# Revit family: BLE-S-WHS-LED
name_source: partatom
category: Lighting Fixtures
units: mm (PartAtom-declared; Revit-internal decimal feet)

## family parameters
Cut with Voids When Loaded = No
Host = Face
Light Source = Yes
Maintain Annotation Orientation = No
Part Type = Normal
Room Calculation Point = No
Round Connector Dimension = Use Diameter
Shared = No

## types (60) — shared parameters
Actual Stem Length = 1' - 0"
Base Material = 100 - Black
Color Filter = 16777215
Default Elevation = 4' - 0"
Dimming Lamp Color Temperature Shift = <None>
Emit from Line Length = 2' - 0"
Length Calc = 1' - 0"
Max Length = 4' - 0"
Min Length = 0' - 6"
Photometric Web File = generic
Shade Material = 100 - Black
Stem Length Multiplier = 2
Stem Material = 100 - Black
Tilt Angle = 0.00°

## per-type parameters (varying)
| type | 12" | 14" | 16" | 18" | 20" | Base Height | CAN-5001 | Dome | Flat | Heat Sink | Light Source Distance | SHD-0189 | STM-50XX | STM-75XX | SUB-0062 |
| 12" Dome 1/2" Stem Swivel Base | Yes | No | No | No | No | 0' - 5 5/32" | No | Yes | No | 0' - 4 5/8" | 0' - 5 5/8" | No | Yes | No | Yes |
| 14" Dome 1/2" Stem Large Base | No | Yes | No | No | No | 0' - 3 11/32" | No | Yes | No | 0' - 4 7/16" | 0' - 5 5/8" | Yes | Yes | No | No |
| 16" Dome 1/2" Stem Large Base | No | No | Yes | No | No | 0' - 3 11/32" | No | Yes | No | 0' - 4 7/16" | 0' - 5 5/8" | Yes | Yes | No | No |
| 18" Dome 1/2" Stem Large Base | No | No | No | Yes | No | 0' - 3 11/32" | No | Yes | No | 0' - 4 13/32" | 0' - 5 5/8" | Yes | Yes | No | No |
| 20" Dome 1/2" Stem Large Base | No | No | No | No | Yes | 0' - 3 11/32" | No | Yes | No | 0' - 4 13/32" | 0' - 5 5/8" | Yes | Yes | No | No |
| 12" Flat 1/2" Stem Large Base | Yes | No | No | No | No | 0' - 3 11/32" | No | No | Yes | 0' - 4 5/8" | 0' - 5 5/8" | Yes | Yes | No | No |
| 14" Flat 1/2" Stem Large Base | No | Yes | No | No | No | 0' - 3 11/32" | No | No | Yes | 0' - 4 7/16" | 0' - 5 5/8" | Yes | Yes | No | No |
| 16" Flat 1/2" Stem Large Base | No | No | Yes | No | No | 0' - 3 11/32" | No | No | Yes | 0' - 4 7/16" | 0' - 5 5/8" | Yes | Yes | No | No |
| 18" Flat 1/2" Stem Large Base | No | No | No | Yes | No | 0' - 3 11/32" | No | No | Yes | 0' - 4 13/32" | 0' - 5 5/8" | Yes | Yes | No | No |
| 20" Flat 1/2" Stem Large Base | No | No | No | No | Yes | 0' - 3 11/32" | No | No | Yes | 0' - 4 13/32" | 0' - 5 5/8" | Yes | Yes | No | No |
| 12" Dome 1/2" Stem Large Base | Yes | No | No | No | No | 0' - 3 11/32" | No | Yes | No | 0' - 4 5/8" | 1' - 10 5/32" | Yes | Yes | No | No |
| 12" Dome 1/2" Stem Small Base | Yes | No | No | No | No | 0' - 0 27/32" | Yes | Yes | No | 0' - 4 5/8" | 1' - 7 3/32" | No | Yes | No | No |
| 12" Flat 1/2" Stem Small Base | Yes | No | No | No | No | 0' - 0 27/32" | Yes | No | Yes | 0' - 4 5/8" | 0' - 5 5/8" | No | Yes | No | No |
| 12" Flat 1/2" Stem Swivel Base | Yes | No | No | No | No | 0' - 5 5/32" | No | No | Yes | 0' - 4 5/8" | 0' - 5 5/8" | No | Yes | No | Yes |
| 14" Dome 1/2" Stem Small Base | No | Yes | No | No | No | 0' - 0 27/32" | Yes | Yes | No | 0' - 4 7/16" | 0' - 5 5/8" | No | Yes | No | No |
| 14" Dome 1/2" Stem Swivel Base | No | Yes | No | No | No | 0' - 5 5/32" | No | Yes | No | 0' - 4 7/16" | 0' - 5 5/8" | No | Yes | No | Yes |
| 14" Flat 1/2" Stem Small Base | No | Yes | No | No | No | 0' - 0 27/32" | Yes | No | Yes | 0' - 4 7/16" | 0' - 5 5/8" | No | Yes | No | No |
| 14" Flat 1/2" Stem Swivel Base | No | Yes | No | No | No | 0' - 5 5/32" | No | No | Yes | 0' - 4 7/16" | 0' - 5 5/8" | No | Yes | No | Yes |
| 16" Dome 1/2" Stem Small Base | No | No | Yes | No | No | 0' - 0 27/32" | Yes | Yes | No | 0' - 4 7/16" | 0' - 5 5/8" | No | Yes | No | No |
| 16" Dome 1/2" Stem Swivel Base | No | No | Yes | No | No | 0' - 5 5/32" | No | Yes | No | 0' - 4 7/16" | 0' - 5 5/8" | No | Yes | No | Yes |
| 16" Flat 1/2" Stem Small Base | No | No | Yes | No | No | 0' - 0 27/32" | Yes | No | Yes | 0' - 4 7/16" | 0' - 5 5/8" | No | Yes | No | No |
| 16" Flat 1/2" Stem Swivel Base | No | No | Yes | No | No | 0' - 5 5/32" | No | No | Yes | 0' - 4 7/16" | 0' - 5 5/8" | No | Yes | No | Yes |
| 18" Dome 1/2" Stem Small Base | No | No | No | Yes | No | 0' - 0 27/32" | Yes | Yes | No | 0' - 4 13/32" | 0' - 5 5/8" | No | Yes | No | No |
| 18" Dome 1/2" Stem Swivel Base | No | No | No | Yes | No | 0' - 5 5/32" | No | Yes | No | 0' - 4 13/32" | 0' - 5 5/8" | No | Yes | No | Yes |
| 18" Flat 1/2" Stem Small Base | No | No | No | Yes | No | 0' - 0 27/32" | Yes | No | Yes | 0' - 4 13/32" | 0' - 5 5/8" | No | Yes | No | No |
| 18" Flat 1/2" Stem Swivel Base | No | No | No | Yes | No | 0' - 5 5/32" | No | No | Yes | 0' - 4 13/32" | 0' - 5 5/8" | No | Yes | No | Yes |
| 20" Dome 1/2" Stem Small Base | No | No | No | No | Yes | 0' - 0 27/32" | Yes | Yes | No | 0' - 4 13/32" | 0' - 5 5/8" | No | Yes | No | No |
| 20" Dome 1/2" Stem Swivel Base | No | No | No | No | Yes | 0' - 5 5/32" | No | Yes | No | 0' - 4 13/32" | 0' - 5 5/8" | No | Yes | No | Yes |
| 20" Flat 1/2" Stem Small Base | No | No | No | No | Yes | 0' - 0 27/32" | Yes | No | Yes | 0' - 4 13/32" | 0' - 5 5/8" | No | Yes | No | No |
| 20" Flat 1/2" Stem Swivel Base | No | No | No | No | Yes | 0' - 5 5/32" | No | No | Yes | 0' - 4 13/32" | 0' - 5 5/8" | No | Yes | No | Yes |
| 12" Dome 3/4" Stem Large Base | Yes | No | No | No | No | 0' - 3 11/32" | No | Yes | No | 0' - 4 5/8" | 1' - 10 5/32" | Yes | No | Yes | No |
| 12" Dome 3/4" Stem Small Base | Yes | No | No | No | No | 0' - 0 27/32" | Yes | Yes | No | 0' - 4 5/8" | 1' - 10 5/32" | No | No | Yes | No |
| 12" Dome 3/4" Stem Swivel Base | Yes | No | No | No | No | 0' - 5 5/32" | No | Yes | No | 0' - 4 5/8" | 1' - 10 5/32" | No | No | Yes | Yes |
| 12" Flat 3/4" Stem Large Base | Yes | No | No | No | No | 0' - 3 11/32" | No | No | Yes | 0' - 4 5/8" | 0' - 5 5/8" | Yes | No | Yes | No |
| 12" Flat 3/4" Stem Small Base | Yes | No | No | No | No | 0' - 0 27/32" | Yes | No | Yes | 0' - 4 5/8" | 0' - 5 5/8" | No | No | Yes | No |
| 12" Flat 3/4" Stem Swivel Base | Yes | No | No | No | No | 0' - 5 5/32" | No | No | Yes | 0' - 4 5/8" | 0' - 5 5/8" | No | No | Yes | Yes |
| 14" Dome 3/4" Stem Large Base | No | Yes | No | No | No | 0' - 3 11/32" | No | Yes | No | 0' - 4 7/16" | 0' - 5 5/8" | Yes | Yes | No | No |
| 14" Dome 3/4" Stem Small Base | No | Yes | No | No | No | 0' - 0 27/32" | Yes | Yes | No | 0' - 4 7/16" | 0' - 5 5/8" | No | No | Yes | No |
| 14" Dome 3/4" Stem Swivel Base | No | Yes | No | No | No | 0' - 5 5/32" | No | Yes | No | 0' - 4 7/16" | 0' - 5 5/8" | No | No | Yes | Yes |
| 14" Flat 3/4" Stem Large Base | No | Yes | No | No | No | 0' - 3 11/32" | No | No | Yes | 0' - 4 7/16" | 0' - 5 5/8" | Yes | No | Yes | No |
| 14" Flat 3/4" Stem Small Base | No | Yes | No | No | No | 0' - 0 27/32" | Yes | No | Yes | 0' - 4 7/16" | 0' - 5 5/8" | No | No | Yes | No |
| 14" Flat 3/4" Stem Swivel Base | No | Yes | No | No | No | 0' - 5 5/32" | No | No | Yes | 0' - 4 7/16" | 0' - 5 5/8" | No | No | Yes | Yes |
| 16" Dome 3/4" Stem Large Base | No | No | Yes | No | No | 0' - 3 11/32" | No | Yes | No | 0' - 4 7/16" | 0' - 5 5/8" | Yes | No | Yes | No |
| 16" Dome 3/4" Stem Small Base | No | No | Yes | No | No | 0' - 0 27/32" | Yes | Yes | No | 0' - 4 7/16" | 0' - 5 5/8" | No | No | Yes | No |
| 16" Dome 3/4" Stem Swivel Base | No | No | Yes | No | No | 0' - 5 5/32" | No | Yes | No | 0' - 4 7/16" | 0' - 5 5/8" | No | No | Yes | Yes |
| 16" Flat 3/4" Stem Large Base | No | No | Yes | No | No | 0' - 3 11/32" | No | No | Yes | 0' - 4 7/16" | 0' - 5 5/8" | Yes | No | Yes | No |
| 16" Flat 3/4" Stem Small Base | No | No | Yes | No | No | 0' - 0 27/32" | Yes | No | Yes | 0' - 4 7/16" | 0' - 5 5/8" | No | No | Yes | No |
| 16" Flat 3/4" Stem Swivel Base | No | No | Yes | No | No | 0' - 5 5/32" | No | No | Yes | 0' - 4 7/16" | 0' - 5 5/8" | No | No | Yes | Yes |
| 18" Dome 3/4" Stem Large Base | No | No | No | Yes | No | 0' - 3 11/32" | No | Yes | No | 0' - 4 13/32" | 0' - 5 5/8" | Yes | No | Yes | No |
| 18" Dome 3/4" Stem Small Base | No | No | No | Yes | No | 0' - 0 27/32" | Yes | Yes | No | 0' - 4 13/32" | 0' - 5 5/8" | No | No | Yes | No |
| 18" Dome 3/4" Stem Swivel Base | No | No | No | Yes | No | 0' - 5 5/32" | No | Yes | No | 0' - 4 13/32" | 0' - 5 5/8" | No | No | Yes | Yes |
| 18" Flat 3/4" Stem Large Base | No | No | No | Yes | No | 0' - 3 11/32" | No | No | Yes | 0' - 4 13/32" | 0' - 5 5/8" | Yes | No | Yes | No |
| 18" Flat 3/4" Stem Small Base | No | No | No | Yes | No | 0' - 0 27/32" | Yes | No | Yes | 0' - 4 13/32" | 0' - 5 5/8" | No | No | Yes | No |
| 18" Flat 3/4" Stem Swivel Base | No | No | No | Yes | No | 0' - 5 5/32" | No | No | Yes | 0' - 4 13/32" | 0' - 5 5/8" | No | No | Yes | Yes |
| 20" Dome 3/4" Stem Large Base | No | No | No | No | Yes | 0' - 3 11/32" | No | Yes | No | 0' - 4 13/32" | 0' - 5 5/8" | Yes | No | Yes | No |
| 20" Dome 3/4" Stem Small Base | No | No | No | No | Yes | 0' - 0 27/32" | Yes | Yes | No | 0' - 4 13/32" | 0' - 5 5/8" | No | No | Yes | No |
| 20" Dome 3/4" Stem Swivel Base | No | No | No | No | Yes | 0' - 5 5/32" | No | Yes | No | 0' - 4 13/32" | 0' - 5 5/8" | No | No | Yes | Yes |
| 20" Flat 3/4" Stem Large Base | No | No | No | No | Yes | 0' - 3 11/32" | No | No | Yes | 0' - 4 13/32" | 0' - 5 5/8" | Yes | No | Yes | No |
| 20" Flat 3/4" Stem Small Base | No | No | No | No | Yes | 0' - 0 27/32" | Yes | No | Yes | 0' - 4 13/32" | 0' - 5 5/8" | No | No | Yes | No |
| 20" Flat 3/4" Stem Swivel Base | No | No | No | No | Yes | 0' - 5 5/32" | No | No | Yes | 0' - 4 13/32" | 0' - 5 5/8" | No | No | Yes | Yes |

## geometry (parser evidence)
native form markers: Sweep x47
no freeform markers — native parametric forms only
